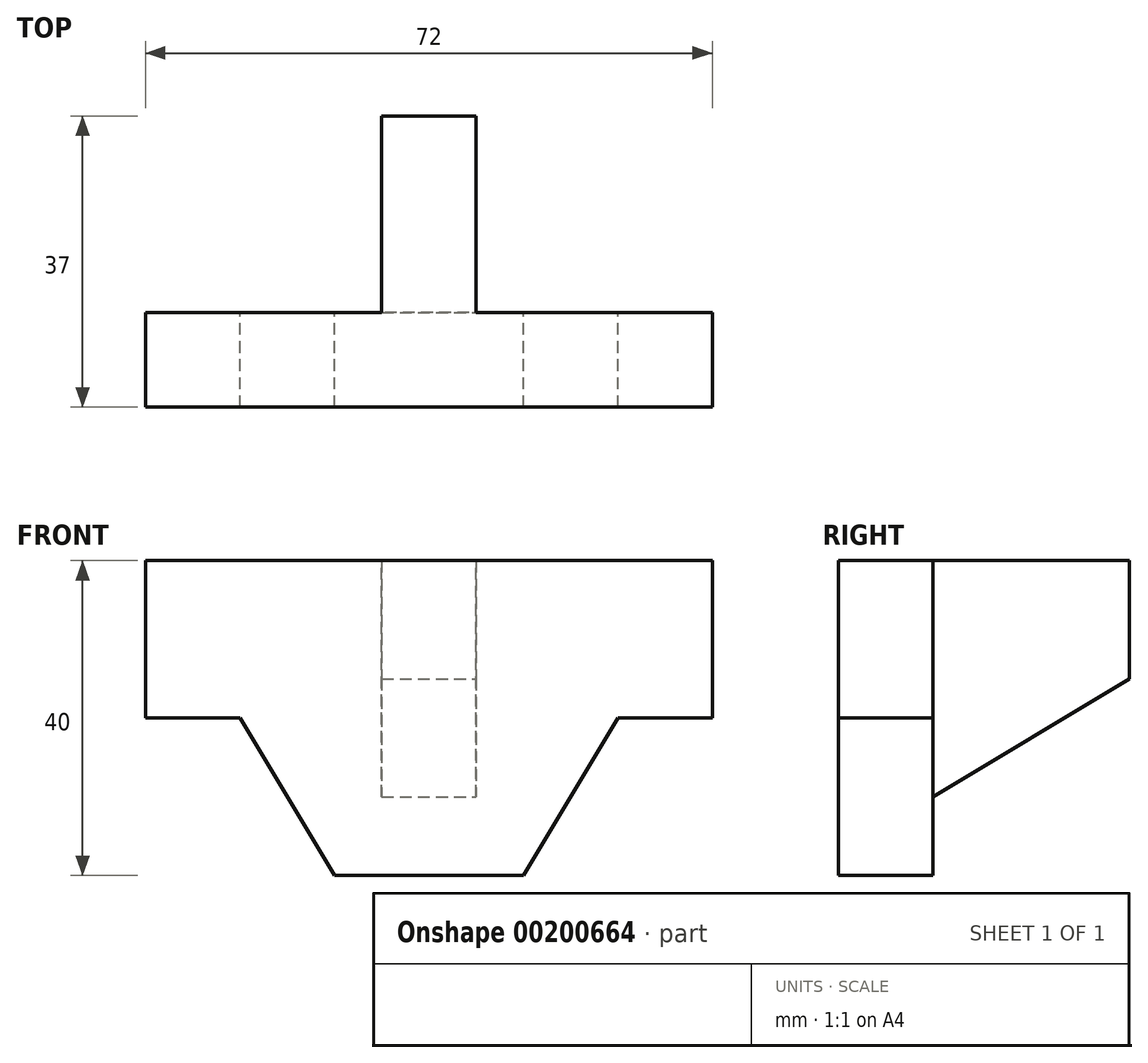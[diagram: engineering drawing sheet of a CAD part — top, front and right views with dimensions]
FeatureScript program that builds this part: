
annotation { "Feature Type Name" : "Feature", "Feature Type Description" : "" }
export const myFeature = defineFeature(function(context is Context, id is Id, definition is map)
    precondition{}
    {
        {
            var Q0;
            Q0=qCreatedBy(makeId("Front.planeOp"),FACE);
            var sketch = newSketch(context, id + "F0", { "sketchPlane" : qUnion([Q0])});
            skLineSegment(sketch, "E0", {"start": v(-36, 0) * mm, "end": v(36, 0) * mm});
            skLineSegment(sketch, "E1", {"start": v(36, 0) * mm, "end": v(36, -20) * mm});
            skLineSegment(sketch, "E2", {"start": v(36, -20) * mm, "end": v(24, -20) * mm});
            skLineSegment(sketch, "E3", {"start": v(24, -20) * mm, "end": v(12, -40) * mm});
            skLineSegment(sketch, "E4", {"start": v(12, -40) * mm, "end": v(-12, -40) * mm});
            skLineSegment(sketch, "E5", {"start": v(-12, -40) * mm, "end": v(-24, -20) * mm});
            skLineSegment(sketch, "E6", {"start": v(-24, -20) * mm, "end": v(-36, -20) * mm});
            skLineSegment(sketch, "E7", {"start": v(-36, -20) * mm, "end": v(-36, 0) * mm});
            skSolve(sketch);
        }
        {
            var Q0;
            Q0=makeQuery(id+"F0.imprint","IMPRINT",FACE,{"disambiguationData":[TD([[makeQuery(id+"F0.imprint","IMPRINT",EDGE,{"derivedFrom":sQuery(id+"F0.wireOp",EDGE,"E0")}),-1.0]])]});
            extrude(context, id + "F1", {"entities" : qUnion([Q0]), "depth" : 12 * mm});
        }
        {
            var Q0;
            Q0=makeQuery(id+"F1.opExtrude","SWEPT_FACE",FACE,{"disambiguationData":[OSD([sQuery(id+"F0.wireOp",EDGE,"E1")])]});
            cPlane(context, id + "F2", {"entities" : qUnion([Q0]), "cplaneType" : CPlaneType.OFFSET, "offset" : 30 * mm, "oppositeDirection" : true, "width" : 150 * mm, "height" : 150 * mm});
        }
        {
            var Q0;
            Q0=qCreatedBy(id+"F2.planeOp",FACE);
            var sketch = newSketch(context, id + "F3", { "sketchPlane" : qUnion([Q0])});
            skLineSegment(sketch, "E8.0.0", {"start": v(0, -20) * mm, "end": v(0, 0) * mm});
            skLineSegment(sketch, "E8.0.1", {"start": v(0, 0) * mm, "end": v(-12, 0) * mm});
            skLineSegment(sketch, "E9", {"start": v(0, 0) * mm, "end": v(25, 0) * mm});
            skLineSegment(sketch, "E10", {"start": v(25, 0) * mm, "end": v(25, -15) * mm});
            skLineSegment(sketch, "E11", {"start": v(25, -15) * mm, "end": v(0, -30) * mm});
            skLineSegment(sketch, "E12", {"start": v(0, -20) * mm, "end": v(0, -30) * mm});
            skSolve(sketch);
        }
        {
            var Q0;
            Q0=makeQuery(id+"F3.imprint","IMPRINT",FACE,{"disambiguationData":[TD([[makeQuery(id+"F3.imprint","IMPRINT",EDGE,{"derivedFrom":sQuery(id+"F3.wireOp",EDGE,"E8.0.0")}),-1.0]])]});
            extrude(context, id + "F4", {"entities" : qUnion([Q0]), "operationType" : NewBodyOperationType.ADD, "oppositeDirection" : true, "depth" : 12 * mm});
        }
    });
